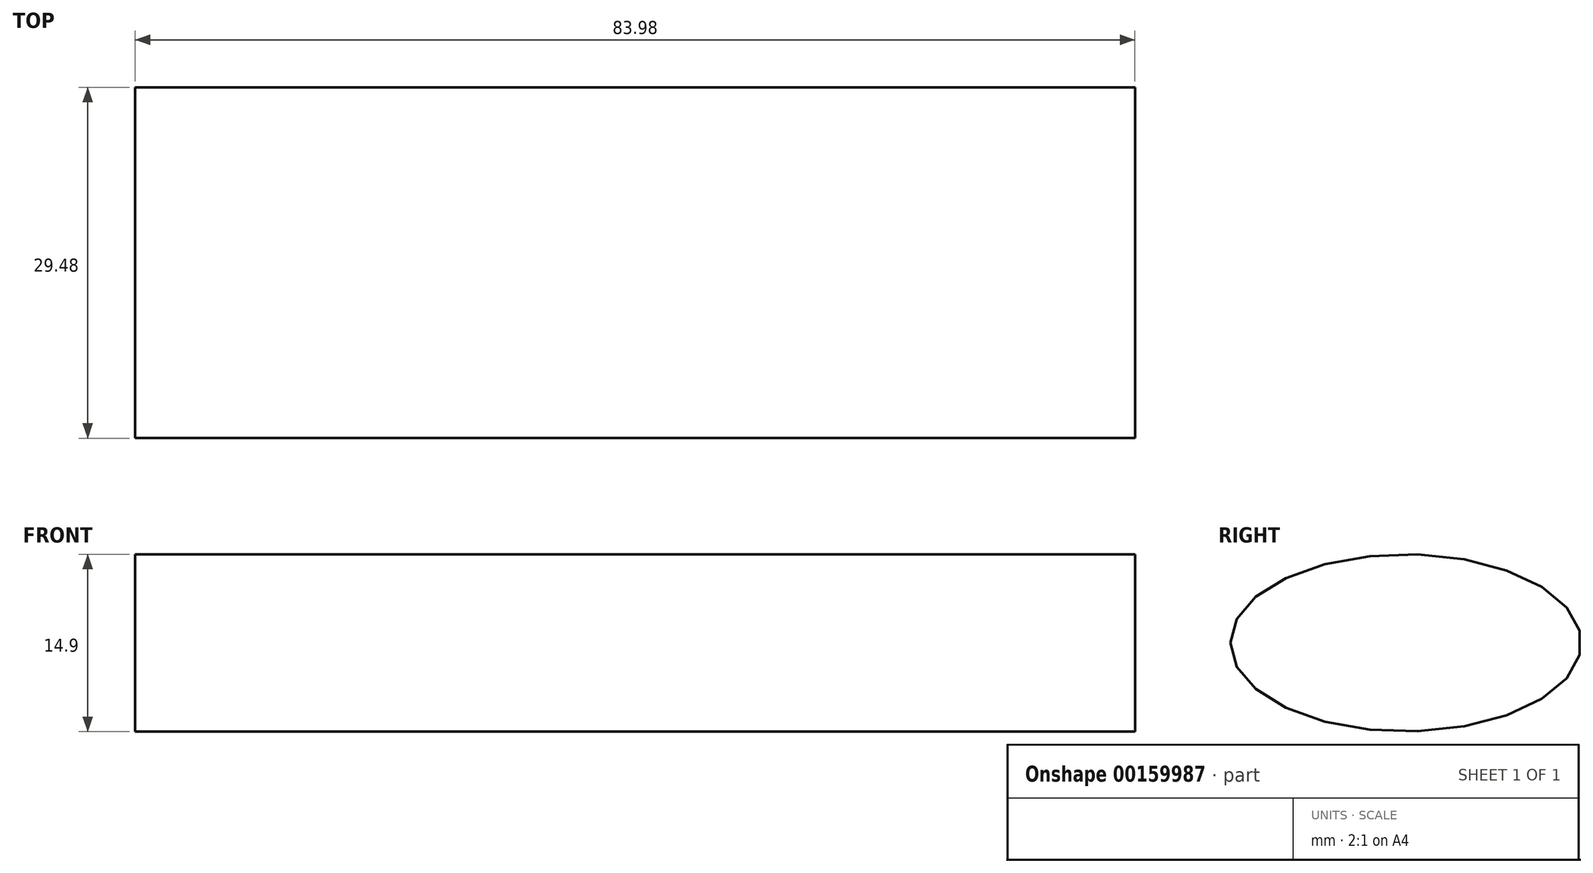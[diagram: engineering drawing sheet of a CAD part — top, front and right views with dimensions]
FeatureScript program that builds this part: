
annotation { "Feature Type Name" : "Feature", "Feature Type Description" : "" }
export const myFeature = defineFeature(function(context is Context, id is Id, definition is map)
    precondition{}
    {
        {
            var Q0;
            Q0=qCreatedBy(makeId("Top.planeOp"),FACE);
            var sketch = newSketch(context, id + "F0", { "sketchPlane" : qUnion([Q0])});
            skLineSegment(sketch, "E0.bottom", {"start": v(-49.52, 42) * mm, "end": v(34.46, 42) * mm});
            skLineSegment(sketch, "E0.top", {"start": v(-49.52, 12.53) * mm, "end": v(34.46, 12.53) * mm});
            skLineSegment(sketch, "E0.left", {"start": v(-49.52, 42) * mm, "end": v(-49.52, 12.53) * mm});
            skLineSegment(sketch, "E0.right", {"start": v(34.46, 42) * mm, "end": v(34.46, 12.53) * mm});
            skSolve(sketch);
        }
        {
            var Q0;
            Q0=makeQuery(id+"F0.imprint","IMPRINT",FACE,{"disambiguationData":[TD([[makeQuery(id+"F0.imprint","IMPRINT",EDGE,{"derivedFrom":sQuery(id+"F0.wireOp",EDGE,"E0.bottom")}),-1.0]])]});
            extrude(context, id + "F1", {"entities" : qUnion([Q0]), "depth" : 25 * mm});
        }
        {
            var Q0;
            Q0=makeQuery(id+"F1.opExtrude","SWEPT_FACE",FACE,{"disambiguationData":[OSD([sQuery(id+"F0.wireOp",EDGE,"E0.left")])]});
            var sketch = newSketch(context, id + "F2", { "sketchPlane" : qUnion([Q0])});
            skLineSegment(sketch, "E1", {"start": v(-27.27, 25) * mm, "end": v(-27.27, 0) * mm, "construction": true});
            skLineSegment(sketch, "E2", {"start": v(-42, 12.5) * mm, "end": v(-12.53, 12.5) * mm, "construction": true});
            skEllipse(sketch, "E3", {"center": v(-27.27, 12.5) * mm, "majorRadius": 14.74 * mm, "minorRadius": 7.45 * mm, "majorAxis": v(1, 0)});
            skSolve(sketch);
        }
        {
            var Q0;
            {var subQ0=sQuery(id+"F2.wireOp",EDGE,"E3");var subQ1=sQuery(id+"F0.wireOp",EDGE,"E0.left");var subQ2=makeQuery(id+"F2.imprint","INTERSECT",VERTEX,{"derivedFrom":[makeQuery(id+"F1.opExtrude","SWEPT_EDGE",EDGE,{"disambiguationData":[OSD([sQuery(id+"F0.wireOp",EDGE,"E0.bottom"),subQ1])]}),subQ0]});Q0=makeQuery(id+"F2.imprint","IMPRINT",FACE,{"disambiguationData":[TD([[makeQuery(id+"F2.imprint","IMPRINT",EDGE,{"disambiguationData":[TD([[subQ2,1.0]])],"derivedFrom":subQ0}),1.0]])]});}
            extrude(context, id + "F3", {"entities" : qUnion([Q0]), "operationType" : NewBodyOperationType.INTERSECT, "oppositeDirection" : true, "depth" : 200 * mm});
        }
    });
